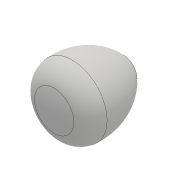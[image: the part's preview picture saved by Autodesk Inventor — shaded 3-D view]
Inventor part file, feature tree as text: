
AUTODESK INVENTOR PART (.ipt)
format: ipt  version: 2017 (Build 210142000, 142)  size: 134,656 bytes
history: native  units: mm
features: fillet x2, revolve x1, sketch x1
ambient origin geometry x8: Origin, YZ Plane, XZ Plane, XY Plane, X Axis, Y Axis, Z Axis, Center Point
bodies: Solid1 (feature_tree)
feature tree (4):
  revolve  "Revolution1"  [1 undecoded]
  fillet  "Fillet1"  Radius=80.0mm
  fillet  "Fillet2"  Radius=4.0mm
  sketch  "Sketch1"  dims[d0=32.0mm d1=32.0mm d2=80.0mm d3=4.0mm d4=90.0deg d5=20.0mm d6=20.0mm]
note: 1 required parameter value undecoded (feature->parameter linkage not recoverable at this tier; creation-order binding heuristic only, values carry confidence <= 0.55)
